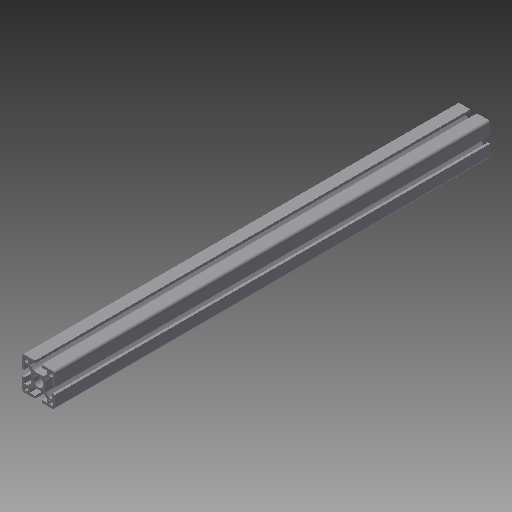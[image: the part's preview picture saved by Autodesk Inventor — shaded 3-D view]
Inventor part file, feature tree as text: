
AUTODESK INVENTOR PART (.ipt)
format: ipt  version: 2018 (Build 220112000, 112)  size: 224,768 bytes
history: native  units: mm
features: other x42, sketch x5, hole x4, extrude x1
ambient origin geometry x8: Origin, YZ Plane, XZ Plane, XY Plane, X Axis, Y Axis, Z Axis, Center Point
bodies: Solid1 (feature_tree)
feature tree (52):
  extrude  "Extrusion1"  [1 undecoded]
  hole  "Drilling 1"  [1 undecoded]
  hole  "Drilling 2"  [1 undecoded]
  hole  "Drilling 3"  [1 undecoded]
  hole  "Drilling 4"  [1 undecoded]
  other  "side_4d_XY"
  other  "side_4d_YZ"
  other  "side_4d_ZX"
  other  "side_4d_X"
  other  "side_4d_Y"
  other  "side_4d_Z"
  other  "side_4d_Center"
  other  "side_1a_XY"
  other  "side_1a_YZ"
  other  "side_1a_ZX"
  other  "side_1a_X"
  other  "side_1a_Y"
  other  "side_1a_Z"
  other  "side_1a_Center"
  other  "side_2b_XY"
  other  "side_2b_YZ"
  other  "side_2b_ZX"
  other  "side_2b_X"
  other  "side_2b_Y"
  other  "side_2b_Z"
  other  "side_2b_Center"
  other  "side_3c_XY"
  other  "side_3c_YZ"
  other  "side_3c_ZX"
  other  "side_3c_X"
  other  "side_3c_Y"
  other  "side_3c_Z"
  other  "side_3c_Center"
  other  "end_XY"
  other  "end_YZ"
  other  "end_ZX"
  other  "end_X"
  other  "end_Y"
  other  "end_Z"
  other  "end_Center"
  other  "start_XY"
  other  "start_YZ"
  other  "start_ZX"
  other  "start_X"
  other  "start_Y"
  other  "start_Z"
  other  "start_Center"
  sketch  "Skizze_1"  dims[d0=529.8mm d1=0.0mm]
  sketch  "Sketch2"  dims[d2=5.0mm d3=6.0mm d4=4.0mm d5=2.0mm d6=90.0deg d7=6000.0mm d8=0.0mm]
  sketch  "Sketch3"  dims[d9=5.0mm d10=6.0mm d11=4.0mm d12=2.0mm d13=90.0deg d14=6000.0mm d15=0.0mm]
  sketch  "Sketch4"  dims[d16=5.0mm d17=6.0mm d18=4.0mm d19=2.0mm d20=90.0deg d21=6000.0mm d22=0.0mm]
  sketch  "Sketch5"  dims[d23=5.0mm d24=6.0mm d25=4.0mm d26=2.0mm d27=90.0deg d28=6000.0mm d29=0.0mm]
note: 5 required parameter values undecoded (feature->parameter linkage not recoverable at this tier; creation-order binding heuristic only, values carry confidence <= 0.55)
